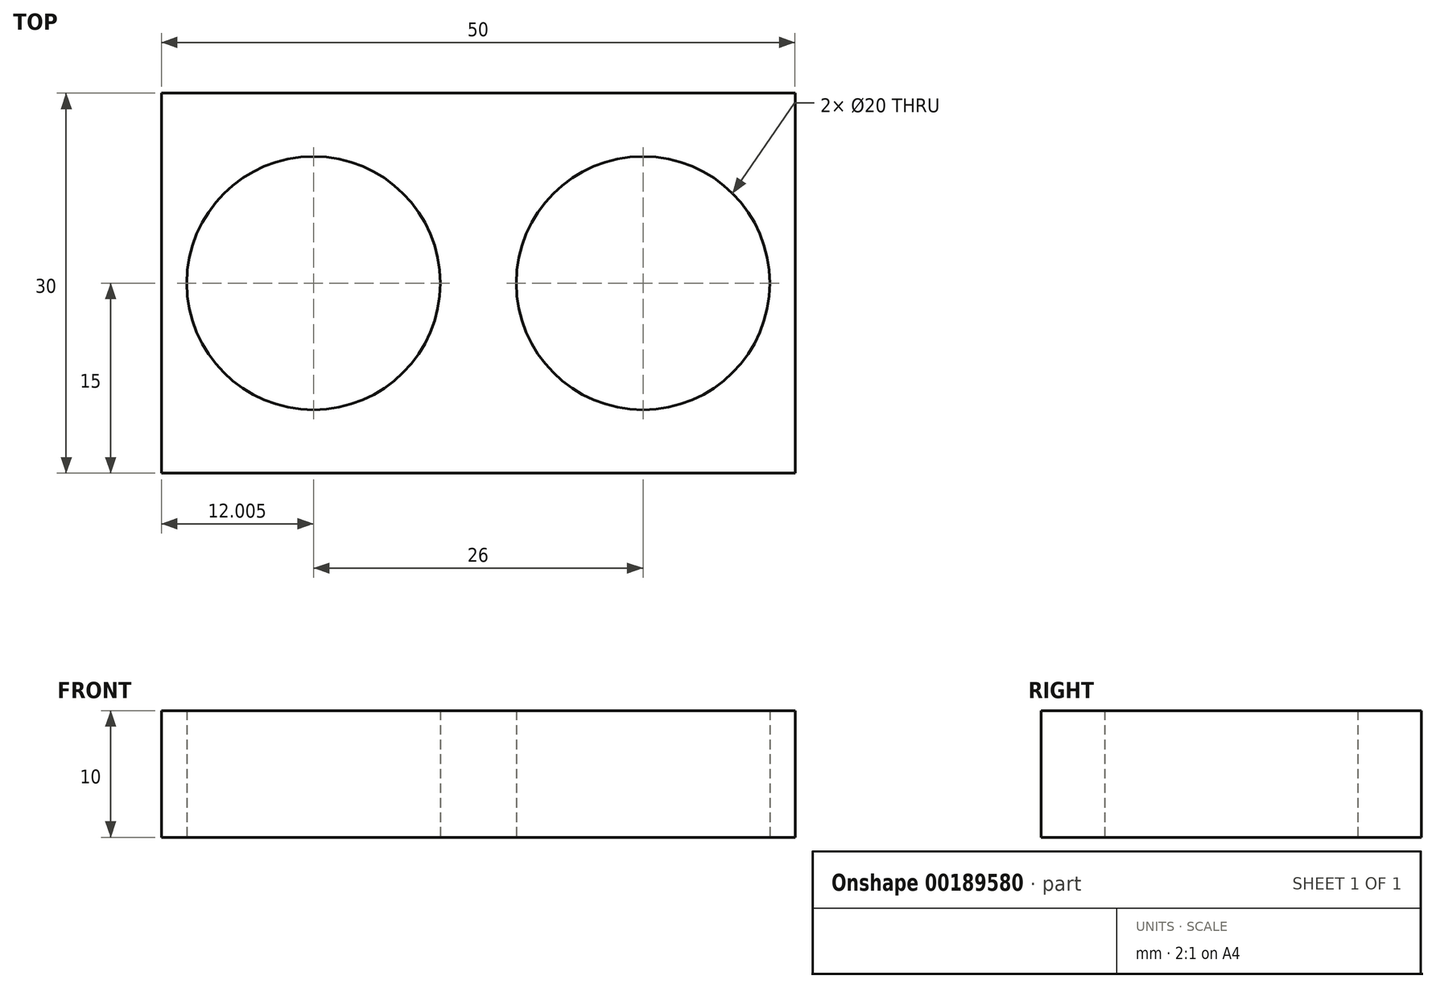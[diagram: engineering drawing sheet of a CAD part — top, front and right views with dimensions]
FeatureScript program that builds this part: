
annotation { "Feature Type Name" : "Feature", "Feature Type Description" : "" }
export const myFeature = defineFeature(function(context is Context, id is Id, definition is map)
    precondition{}
    {
        {
            var Q0;
            Q0=qCreatedBy(makeId("Top.planeOp"),FACE);
            var sketch = newSketch(context, id + "F0", { "sketchPlane" : qUnion([Q0])});
            skLineSegment(sketch, "E0.bottom", {"start": v(-32.99, 15) * mm, "end": v(17.01, 15) * mm});
            skLineSegment(sketch, "E0.top", {"start": v(-32.99, -15) * mm, "end": v(17.01, -15) * mm});
            skLineSegment(sketch, "E0.left", {"start": v(-32.99, 15) * mm, "end": v(-32.99, -15) * mm});
            skLineSegment(sketch, "E0.right", {"start": v(17.01, 15) * mm, "end": v(17.01, -15) * mm});
            skCircle(sketch, "E1", {"center": v(5.01, 0) * mm, "radius": 10 * mm});
            skCircle(sketch, "E2", {"center": v(-20.99, 0) * mm, "radius": 10 * mm});
            skSolve(sketch);
        }
        {
            var Q0;
            Q0=makeQuery(id+"F0.imprint","IMPRINT",FACE,{"disambiguationData":[TD([[makeQuery(id+"F0.imprint","IMPRINT",EDGE,{"derivedFrom":sQuery(id+"F0.wireOp",EDGE,"E0.bottom")}),-1.0]])]});
            extrude(context, id + "F1", {"entities" : qUnion([Q0]), "depth" : 10 * mm});
        }
    });
